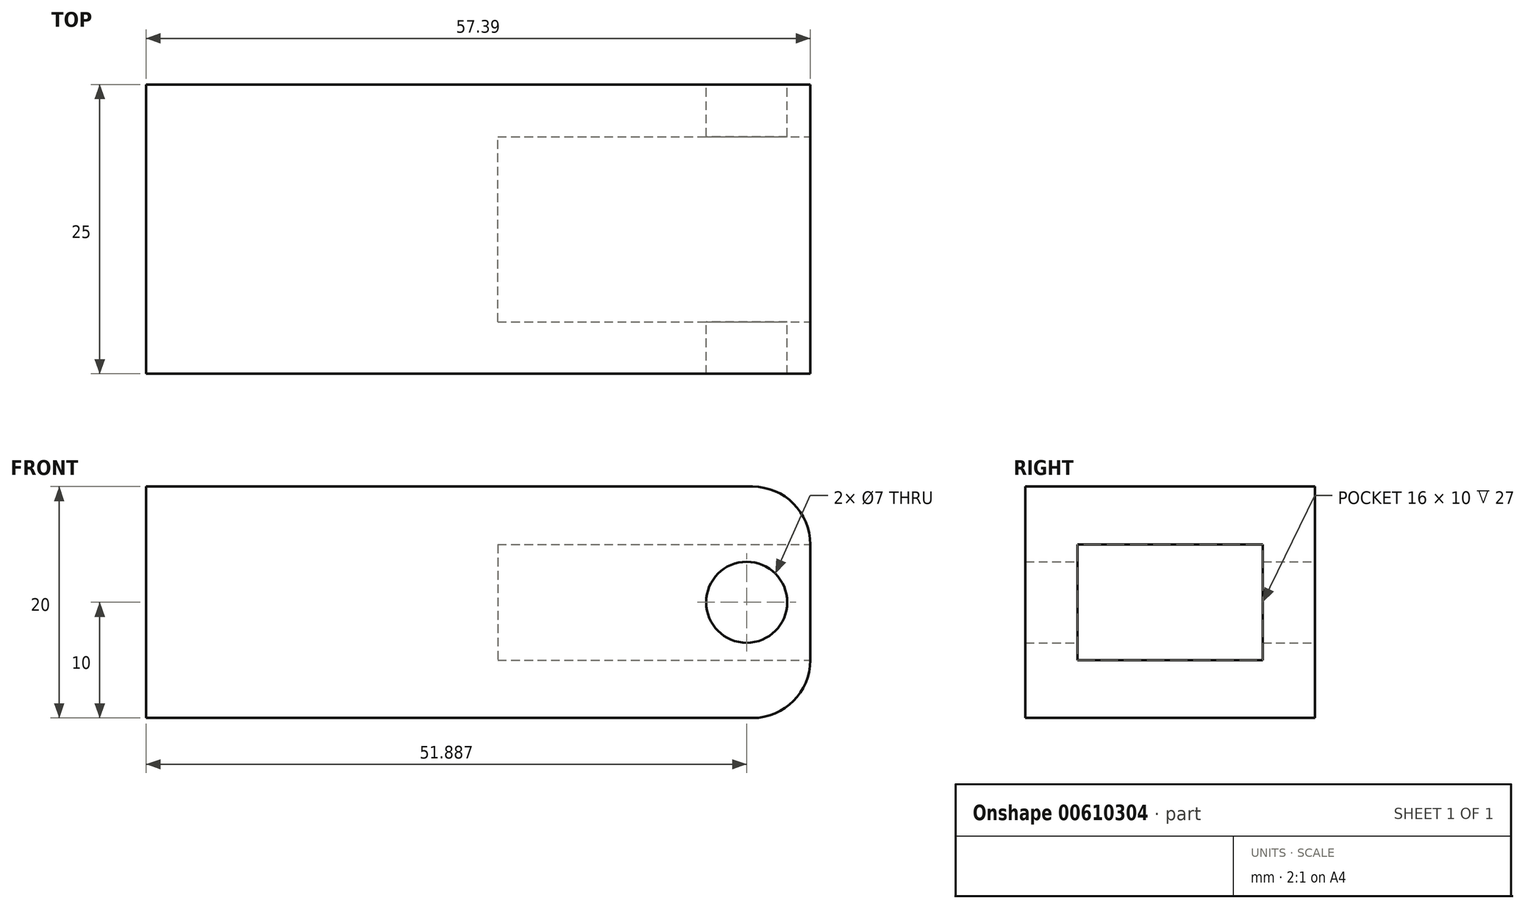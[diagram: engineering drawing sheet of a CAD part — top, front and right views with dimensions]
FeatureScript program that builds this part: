
annotation { "Feature Type Name" : "Feature", "Feature Type Description" : "" }
export const myFeature = defineFeature(function(context is Context, id is Id, definition is map)
    precondition{}
    {
        {
            var Q0;
            Q0=qCreatedBy(makeId("Front.planeOp"),FACE);
            var sketch = newSketch(context, id + "F0", { "sketchPlane" : qUnion([Q0])});
            skLineSegment(sketch, "E0", {"start": v(57.39, 15) * mm, "end": v(57.39, 5) * mm});
            skCircle(sketch, "E1", {"center": v(51.89, 10) * mm, "radius": 3.5 * mm});
            skLineSegment(sketch, "E2", {"start": v(40, 20) * mm, "end": v(40, 0) * mm, "construction": true});
            skPoint(sketch, "E3.visualSharp", {"position": v(57.39, 21.24) * mm});
            skArc(sketch, "E3.filletArc", {"start": v(57.39, 15) * mm, "mid": v(55.92, 18.54) * mm, "end": v(52.39, 20) * mm});
            skPoint(sketch, "E4.visualSharp", {"position": v(57.39, 1.24) * mm});
            skArc(sketch, "E4.filletArc", {"start": v(52.39, 0) * mm, "mid": v(55.92, 1.46) * mm, "end": v(57.39, 5) * mm});
            skLineSegment(sketch, "E5", {"start": v(0, 0) * mm, "end": v(0, 20) * mm});
            skLineSegment(sketch, "E6", {"start": v(51.89, 10) * mm, "end": v(0, 10) * mm, "construction": true});
            skPoint(sketch, "E6.endSnap0", {"position": v(0, 10) * mm});
            skLineSegment(sketch, "E7", {"start": v(0, 20) * mm, "end": v(52.39, 20) * mm});
            skLineSegment(sketch, "E8", {"start": v(0, 0) * mm, "end": v(52.39, 0) * mm});
            skLineSegment(sketch, "E9", {"start": v(55.39, 10.03) * mm, "end": v(57.39, 10.03) * mm, "construction": true});
            skLineSegment(sketch, "E10", {"start": v(51.89, 10) * mm, "end": v(51.89, 0) * mm, "construction": true});
            skLineSegment(sketch, "E11", {"start": v(51.89, 10) * mm, "end": v(51.89, 20) * mm, "construction": true});
            skLineSegment(sketch, "E12", {"start": v(0, 0.25) * mm, "end": v(0, -0.07) * mm, "construction": true});
            skLineSegment(sketch, "E13", {"start": v(-0.08, 0) * mm, "end": v(0.07, 0) * mm, "construction": true});
            skSolve(sketch);
        }
        {
            var Q0;
            Q0=makeQuery(id+"F0.imprint","IMPRINT",FACE,{"disambiguationData":[TD([[makeQuery(id+"F0.imprint","IMPRINT",EDGE,{"derivedFrom":sQuery(id+"F0.wireOp",EDGE,"E0")}),-1.0]])]});
            extrude(context, id + "F1", {"entities" : qUnion([Q0]), "endBound" : BoundingType.SYMMETRIC, "depth" : 25 * mm, "offsetDistance" : 25 * mm});
        }
        {
            var Q0;
            Q0=makeQuery(id+"F1.opExtrude","SWEPT_FACE",FACE,{"disambiguationData":[OSD([sQuery(id+"F0.wireOp",EDGE,"E0")])]});
            var sketch = newSketch(context, id + "F2", { "sketchPlane" : qUnion([Q0])});
            skLineSegment(sketch, "E14.0", {"start": v(-12.5, 20) * mm, "end": v(12.5, 20) * mm});
            skLineSegment(sketch, "E15.0", {"start": v(-12.5, 0) * mm, "end": v(12.5, 0) * mm});
            skLineSegment(sketch, "E16.0", {"start": v(-12.5, 15) * mm, "end": v(-12.5, 20) * mm});
            skLineSegment(sketch, "E17.0", {"start": v(12.5, 15) * mm, "end": v(12.5, 20) * mm});
            skLineSegment(sketch, "E18.0", {"start": v(12.5, 0) * mm, "end": v(12.5, 5) * mm});
            skLineSegment(sketch, "E19.0", {"start": v(-12.5, 0) * mm, "end": v(-12.5, 5) * mm});
            skLineSegment(sketch, "E20.0", {"start": v(-12.5, 15) * mm, "end": v(-12.5, 5) * mm});
            skLineSegment(sketch, "E21.0", {"start": v(12.5, 15) * mm, "end": v(12.5, 5) * mm});
            skLineSegment(sketch, "E22", {"start": v(0, 20) * mm, "end": v(0, 0) * mm});
            skLineSegment(sketch, "E23", {"start": v(0, 20) * mm, "end": v(-8, 20) * mm});
            skLineSegment(sketch, "E24", {"start": v(-8, 20) * mm, "end": v(-8, 0) * mm});
            skLineSegment(sketch, "E25", {"start": v(-8, 0) * mm, "end": v(0, 0) * mm});
            skLineSegment(sketch, "E26", {"start": v(0, 0) * mm, "end": v(8, 0) * mm});
            skLineSegment(sketch, "E27", {"start": v(8, 0) * mm, "end": v(8, 20) * mm});
            skLineSegment(sketch, "E28", {"start": v(8, 20) * mm, "end": v(0, 20) * mm});
            skLineSegment(sketch, "E29", {"start": v(-12.5, 20) * mm, "end": v(-12.5, 21.48) * mm});
            skLineSegment(sketch, "E30", {"start": v(-12.5, 21.48) * mm, "end": v(0, 21.48) * mm});
            skLineSegment(sketch, "E31", {"start": v(0, 21.48) * mm, "end": v(12.5, 20) * mm});
            skSolve(sketch);
        }
        {
            var Q0;
            {var subQ0=sQuery(id+"F2.wireOp",EDGE,"E23");Q0=makeQuery(id+"F2.imprint","IMPRINT",FACE,{"disambiguationData":[TD([[makeQuery(id+"F2.imprint","IMPRINT",EDGE,{"derivedFrom":subQ0}),1.0]])]});}
            var Q1;
            {var subQ0=sQuery(id+"F2.wireOp",EDGE,"E28");Q1=makeQuery(id+"F2.imprint","IMPRINT",FACE,{"disambiguationData":[TD([[makeQuery(id+"F2.imprint","IMPRINT",EDGE,{"derivedFrom":subQ0}),1.0]])]});}
            var Q2;
            {var subQ0=sQuery(id+"F2.wireOp",EDGE,"E22");var subQ1=sQuery(id+"F0.wireOp",EDGE,"E0");var subQ2=makeQuery(id+"F1.opExtrude","SWEPT_EDGE",EDGE,{"disambiguationData":[OSD([subQ1,sQuery(id+"F0.wireOp",EDGE,"E3.filletArc")])]});var subQ3=makeQuery(id+"F2.imprint","INTERSECT",VERTEX,{"derivedFrom":[subQ2,subQ0]});Q2=makeQuery(id+"F2.imprint","IMPRINT",FACE,{"disambiguationData":[TD([[makeQuery(id+"F2.imprint","IMPRINT",EDGE,{"disambiguationData":[TD([[subQ3,-1.0]])],"derivedFrom":subQ0}),1.0]])]});}
            var Q3;
            {var subQ0=sQuery(id+"F2.wireOp",EDGE,"E22");var subQ1=sQuery(id+"F0.wireOp",EDGE,"E0");var subQ2=makeQuery(id+"F1.opExtrude","SWEPT_EDGE",EDGE,{"disambiguationData":[OSD([subQ1,sQuery(id+"F0.wireOp",EDGE,"E3.filletArc")])]});var subQ3=makeQuery(id+"F2.imprint","INTERSECT",VERTEX,{"derivedFrom":[subQ2,subQ0]});Q3=makeQuery(id+"F2.imprint","IMPRINT",FACE,{"disambiguationData":[TD([[makeQuery(id+"F2.imprint","IMPRINT",EDGE,{"disambiguationData":[TD([[subQ3,-1.0]])],"derivedFrom":subQ0}),-1.0]])]});}
            var Q4;
            {var subQ0=sQuery(id+"F2.wireOp",EDGE,"E25");Q4=makeQuery(id+"F2.imprint","IMPRINT",FACE,{"disambiguationData":[TD([[makeQuery(id+"F2.imprint","IMPRINT",EDGE,{"derivedFrom":subQ0}),1.0]])]});}
            var Q5;
            {var subQ0=sQuery(id+"F2.wireOp",EDGE,"E26");Q5=makeQuery(id+"F2.imprint","IMPRINT",FACE,{"disambiguationData":[TD([[makeQuery(id+"F2.imprint","IMPRINT",EDGE,{"derivedFrom":subQ0}),1.0]])]});}
            var Q6;
            {var subQ8=sQuery(id+"F2.wireOp",EDGE,"E23");Q6=makeQuery(id+"F2.imprint","IMPRINT",FACE,{"disambiguationData":[TD([[makeQuery(id+"F2.imprint","IMPRINT",EDGE,{"derivedFrom":subQ8}),-1.0]])]});}
            extrude(context, id + "F3", {"entities" : qUnion([Q0, Q1, Q2, Q3, Q4, Q5, Q6]), "operationType" : NewBodyOperationType.REMOVE, "oppositeDirection" : true, "depth" : 27 * mm, "offsetDistance" : 25 * mm});
        }
    });
